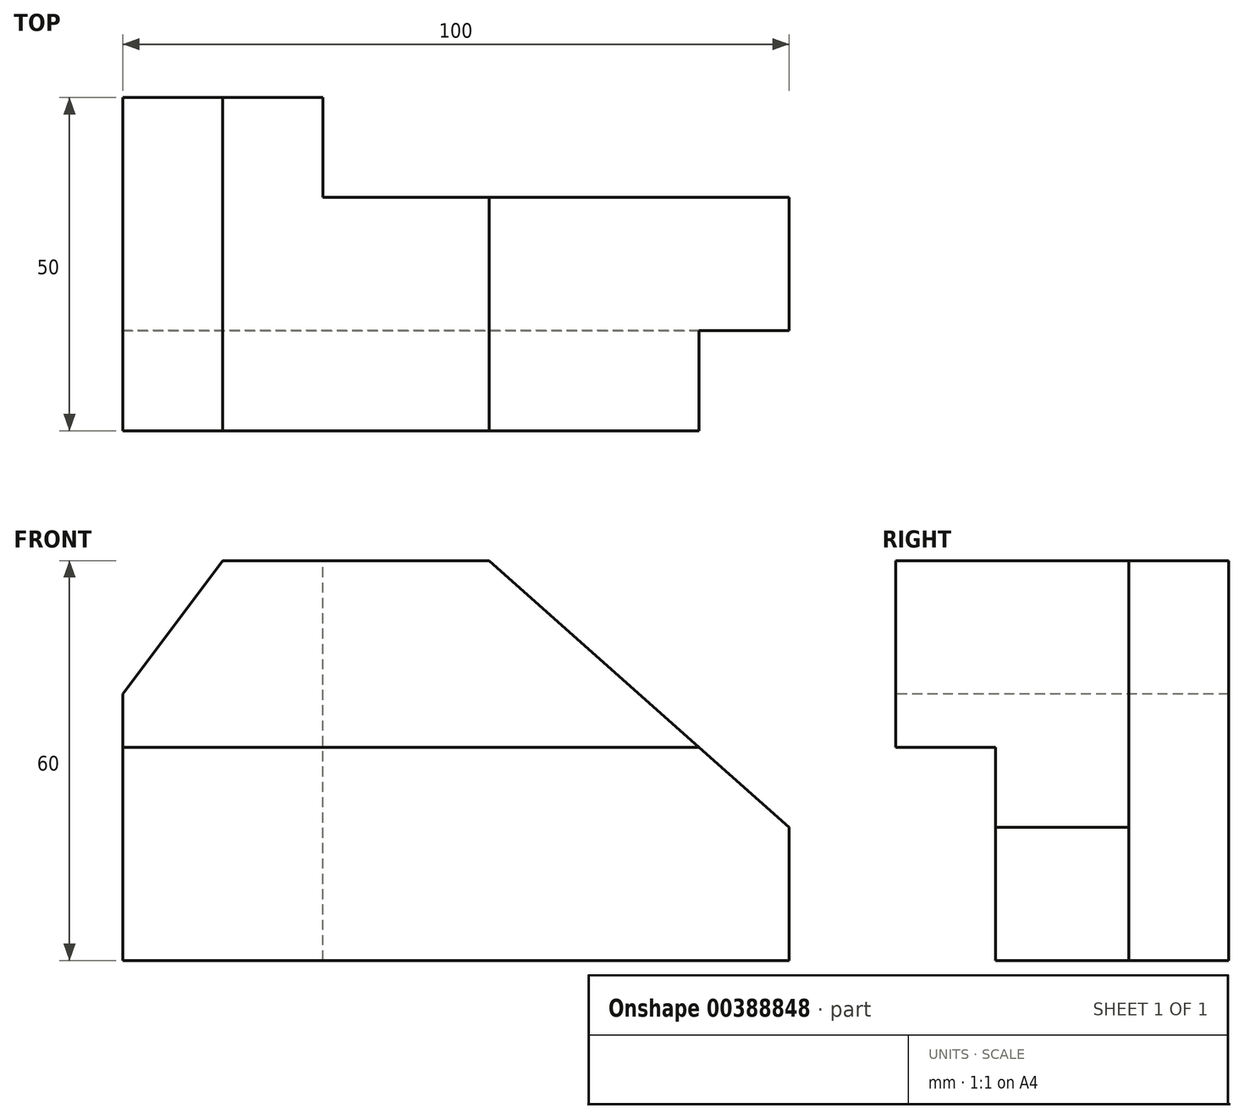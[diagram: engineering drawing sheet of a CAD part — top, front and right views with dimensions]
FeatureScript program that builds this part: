
annotation { "Feature Type Name" : "Feature", "Feature Type Description" : "" }
export const myFeature = defineFeature(function(context is Context, id is Id, definition is map)
    precondition{}
    {
        {
            var Q0;
            Q0=qCreatedBy(makeId("Top.planeOp"),FACE);
            var sketch = newSketch(context, id + "F0", { "sketchPlane" : qUnion([Q0])});
            skLineSegment(sketch, "E0.bottom", {"start": v(0, 0) * mm, "end": v(100, 0) * mm});
            skLineSegment(sketch, "E0.top", {"start": v(0, 50) * mm, "end": v(100, 50) * mm});
            skLineSegment(sketch, "E0.left", {"start": v(0, 0) * mm, "end": v(0, 50) * mm});
            skLineSegment(sketch, "E0.right", {"start": v(100, 0) * mm, "end": v(100, 50) * mm});
            skSolve(sketch);
        }
        {
            var Q0;
            Q0 = qSketchRegion(id + "F0", true);
            extrude(context, id + "F1", {"entities" : qUnion([Q0]), "depth" : 60 * mm});
        }
        {
            var Q0;
            Q0=makeQuery(id+"F1.opExtrude","SWEPT_FACE",FACE,{"disambiguationData":[OSD([sQuery(id+"F0.wireOp",EDGE,"E0.bottom")])]});
            var sketch = newSketch(context, id + "F2", { "sketchPlane" : qUnion([Q0])});
            skLineSegment(sketch, "E1", {"start": v(0, 60) * mm, "end": v(15, 60) * mm});
            skLineSegment(sketch, "E2", {"start": v(15, 60) * mm, "end": v(0, 40) * mm});
            skSolve(sketch);
        }
        {
            var Q0;
            {var subQ0=sQuery(id+"F2.wireOp",EDGE,"E1");Q0=makeQuery(id+"F2.imprint","IMPRINT",FACE,{"disambiguationData":[TD([[makeQuery(id+"F2.imprint","IMPRINT",EDGE,{"derivedFrom":subQ0}),-1.0]])]});}
            extrude(context, id + "F3", {"entities" : qUnion([Q0]), "operationType" : NewBodyOperationType.REMOVE, "endBound" : BoundingType.UP_TO_NEXT, "oppositeDirection" : true, "depth" : 25 * mm});
        }
        {
            var Q0;
            Q0=makeQuery(id+"F1.opExtrude","SWEPT_FACE",FACE,{"disambiguationData":[OSD([sQuery(id+"F0.wireOp",EDGE,"E0.bottom")])]});
            var sketch = newSketch(context, id + "F4", { "sketchPlane" : qUnion([Q0])});
            skLineSegment(sketch, "E3", {"start": v(100, 60) * mm, "end": v(55, 60) * mm});
            skLineSegment(sketch, "E4", {"start": v(55, 60) * mm, "end": v(100, 20) * mm});
            skSolve(sketch);
        }
        {
            var Q0;
            {var subQ0=sQuery(id+"F4.wireOp",EDGE,"E3");Q0=makeQuery(id+"F4.imprint","IMPRINT",FACE,{"disambiguationData":[TD([[makeQuery(id+"F4.imprint","IMPRINT",EDGE,{"derivedFrom":subQ0}),-1.0]])]});}
            extrude(context, id + "F5", {"entities" : qUnion([Q0]), "operationType" : NewBodyOperationType.REMOVE, "endBound" : BoundingType.UP_TO_NEXT, "oppositeDirection" : true, "depth" : 25 * mm});
        }
        {
            var Q0;
            Q0=makeQuery(id+"F1.opExtrude","SWEPT_FACE",FACE,{"disambiguationData":[OSD([sQuery(id+"F0.wireOp",EDGE,"E0.top")])]});
            var sketch = newSketch(context, id + "F6", { "sketchPlane" : qUnion([Q0])});
            skLineSegment(sketch, "E5", {"start": v(0, 0) * mm, "end": v(-30, 0) * mm});
            skLineSegment(sketch, "E6", {"start": v(-30, 0) * mm, "end": v(-30, 60) * mm});
            skLineSegment(sketch, "E7", {"start": v(-30, 0) * mm, "end": v(-100, 0) * mm});
            skLineSegment(sketch, "E8", {"start": v(-100, 0) * mm, "end": v(-100, 20) * mm});
            skLineSegment(sketch, "E9", {"start": v(-100, 20) * mm, "end": v(-55, 60) * mm});
            skLineSegment(sketch, "E10", {"start": v(-55, 60) * mm, "end": v(-30, 60) * mm});
            skSolve(sketch);
        }
        {
            var Q0;
            Q0=makeQuery(id+"F6.imprint","IMPRINT",FACE,{"disambiguationData":[TD([[makeQuery(id+"F6.imprint","IMPRINT",EDGE,{"derivedFrom":sQuery(id+"F6.wireOp",EDGE,"E6")}),1.0]])]});
            extrude(context, id + "F7", {"entities" : qUnion([Q0]), "operationType" : NewBodyOperationType.REMOVE, "oppositeDirection" : true, "depth" : 15 * mm});
        }
        {
            var Q0;
            Q0=makeQuery(id+"F1.opExtrude","SWEPT_FACE",FACE,{"disambiguationData":[OSD([sQuery(id+"F0.wireOp",EDGE,"E0.bottom")])]});
            var sketch = newSketch(context, id + "F8", { "sketchPlane" : qUnion([Q0])});
            skLineSegment(sketch, "E11", {"start": v(0, 0) * mm, "end": v(0, 32) * mm});
            skLineSegment(sketch, "E12", {"start": v(0, 32) * mm, "end": v(86.5, 32) * mm});
            skLineSegment(sketch, "E13", {"start": v(86.5, 32) * mm, "end": v(86.5, 0) * mm});
            skSolve(sketch);
        }
        {
            var Q0;
            {var subQ0=sQuery(id+"F8.wireOp",EDGE,"E13");Q0=makeQuery(id+"F8.imprint","IMPRINT",FACE,{"disambiguationData":[TD([[makeQuery(id+"F8.imprint","IMPRINT",EDGE,{"derivedFrom":subQ0}),1.0]])]});}
            extrude(context, id + "F9", {"entities" : qUnion([Q0]), "operationType" : NewBodyOperationType.REMOVE, "oppositeDirection" : true, "depth" : 15 * mm});
        }
        {
            var Q0;
            Q0=makeQuery(id+"F1.opExtrude","SWEPT_FACE",FACE,{"disambiguationData":[OSD([sQuery(id+"F0.wireOp",EDGE,"E0.bottom")])]});
            var sketch = newSketch(context, id + "F10", { "sketchPlane" : qUnion([Q0])});
            skLineSegment(sketch, "E14", {"start": v(86.5, 32) * mm, "end": v(0, 32) * mm});
            skSolve(sketch);
        }
        {
            var Q0;
            {var subQ0=sQuery(id+"F10.wireOp",EDGE,"E14");Q0=makeQuery(id+"F10.imprint","IMPRINT",FACE,{"disambiguationData":[TD([[makeQuery(id+"F10.imprint","IMPRINT",EDGE,{"derivedFrom":subQ0}),1.0]])]});}
            extrude(context, id + "F11", {"entities" : qUnion([Q0]), "operationType" : NewBodyOperationType.REMOVE, "oppositeDirection" : true, "depth" : 15 * mm});
        }
    });
